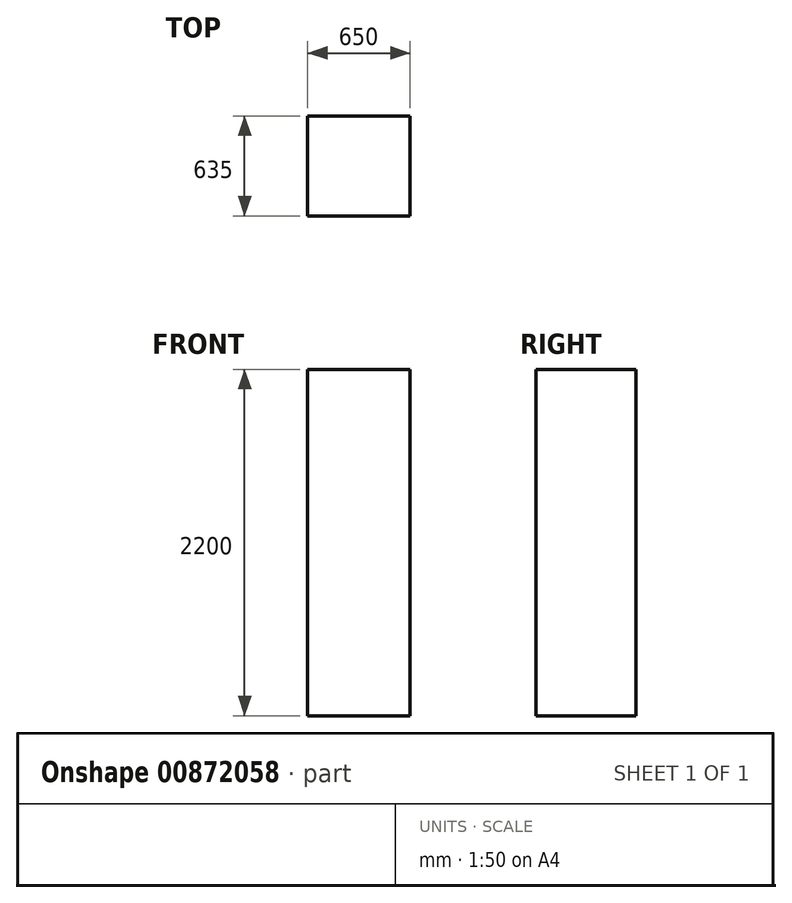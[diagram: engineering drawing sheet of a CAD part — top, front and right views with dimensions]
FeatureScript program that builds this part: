
annotation { "Feature Type Name" : "Feature", "Feature Type Description" : "" }
export const myFeature = defineFeature(function(context is Context, id is Id, definition is map)
    precondition{}
    {
        {
            var Q0;
            Q0=qCreatedBy(makeId("Top.planeOp"),FACE);
            var sketch = newSketch(context, id + "F0", { "sketchPlane" : qUnion([Q0])});
            skLineSegment(sketch, "E0.bottom", {"start": v(0, 0) * mm, "end": v(650, 0) * mm});
            skLineSegment(sketch, "E0.top", {"start": v(0, 635) * mm, "end": v(650, 635) * mm});
            skLineSegment(sketch, "E0.left", {"start": v(0, 0) * mm, "end": v(0, 635) * mm});
            skLineSegment(sketch, "E0.right", {"start": v(650, 0) * mm, "end": v(650, 635) * mm});
            skSolve(sketch);
        }
        {
            var Q0;
            Q0=makeQuery(id+"F0.imprint","IMPRINT",FACE,{"disambiguationData":[TD([[makeQuery(id+"F0.imprint","IMPRINT",EDGE,{"derivedFrom":sQuery(id+"F0.wireOp",EDGE,"E0.bottom")}),1.0]])]});
            extrude(context, id + "F1", {"entities" : qUnion([Q0]), "depth" : 2200 * mm, "offsetDistance" : 25 * mm});
        }
    });
